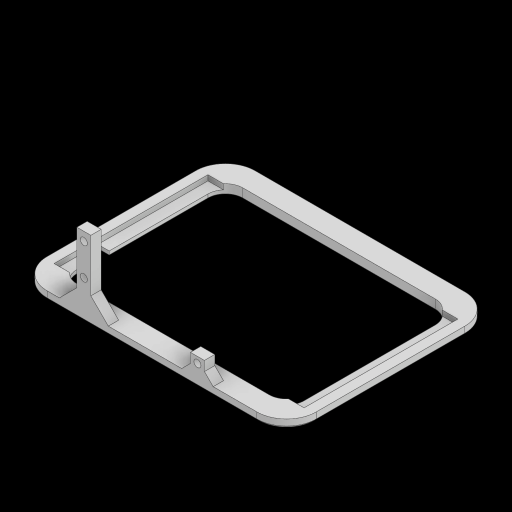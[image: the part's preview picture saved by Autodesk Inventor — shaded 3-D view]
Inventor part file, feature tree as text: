
AUTODESK INVENTOR PART (.ipt)
format: ipt  version: 2024 (Build 280153000, 153)  size: 229,376 bytes
history: native  units: mm
features: extrude x7, sketch x7, chamfer x3, fillet x1
ambient origin geometry x8: Origin, YZ Plane, XZ Plane, XY Plane, X Axis, Y Axis, Z Axis, Center Point
bodies: Volumenkörper1 (feature_tree)
feature tree (18):
  extrude  "Extrusion1"  Depth=119.0mm
  fillet  "Rundung1"  Radius=5.0mm
  chamfer  "Fasen1"  Distance=1.5mm Angle=45.0deg
  extrude  "Extrusion2"  Depth=10.0mm
  extrude  "Extrusion3"  Depth=10.0mm
  extrude  "Extrusion5"  Depth=130.0mm
  chamfer  "Fasen2"  Distance=3.0mm
  extrude  "Extrusion6"  Depth=143.0mm
  chamfer  "Fasen3"  Distance=88.0mm
  extrude  "Extrusion7"  Depth=3.0mm TaperAngle=0.0deg
  extrude  "Extrusion8"  Depth=5.0mm
  sketch  "Skizze1"  dims[d0=154.0mm d1=119.0mm d2=5.0mm d3=0.0mm]
  sketch  "Skizze2"  dims[d4=17.0mm d5=1.5mm d6=2.0mm d7=45.0deg]
  sketch  "Skizze3"  dims[d10=10.0mm d11=10.0mm]
  sketch  "Skizze5"  dims[d12=10.0mm d13=10.0mm]
  sketch  "Skizze6"  dims[d14=95.0mm d15=130.0mm]
  sketch  "Skizze7"  dims[d16=154.0mm]
  sketch  "Skizze8"  dims[d17=119.0mm d18=3.0mm d19=0.0mm d20=143.0mm d21=88.0mm d22=3.0mm d23=0.0mm d29=38.0mm d30=5.9mm d31=8.0mm d32=40.0mm d33=0.0mm d34=10.0mm d35=2.0mm d36=45.0deg d37=103.0mm d38=8.0mm d39=5.9mm d40=10.5mm d41=0.0mm d42=5.0mm d43=2.0mm d44=45.0deg d45=21.0mm d46=8.0mm d48=5.0mm d49=3.0mm d50=0.0mm d51=4.0mm d52=5.0mm d53=4.0mm d54=18.0mm d55=4.0mm d56=33.0mm d57=0.0mm d58=0.0mm d59=0.0mm]
